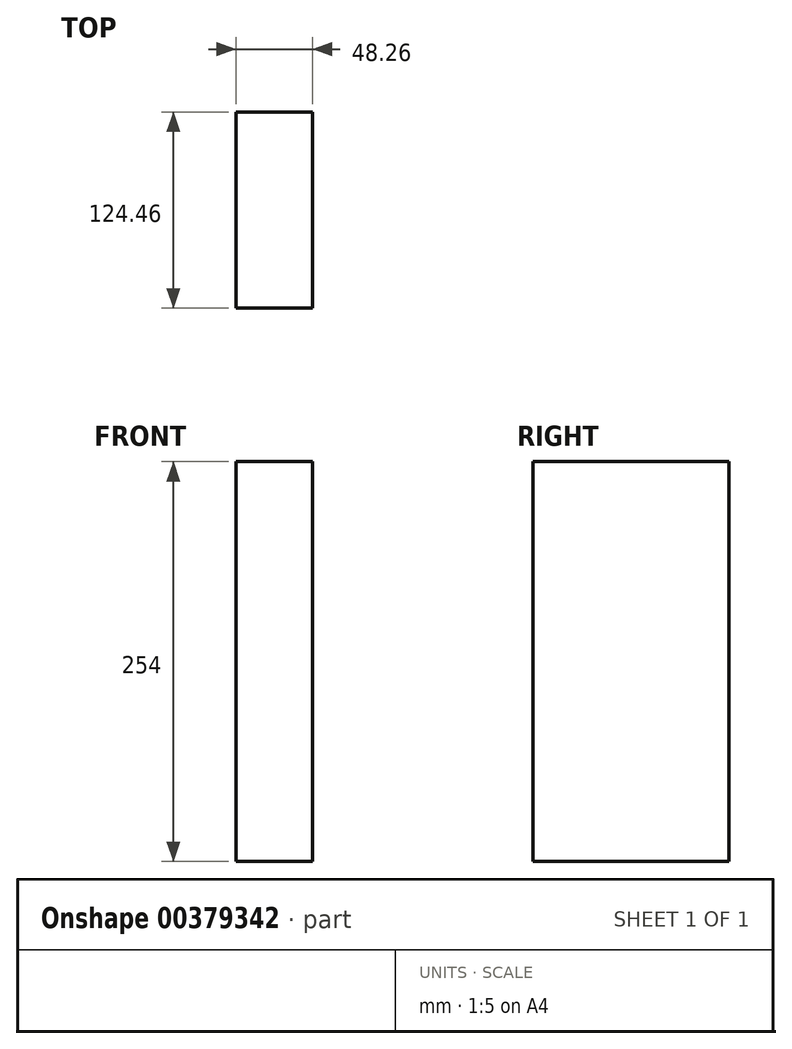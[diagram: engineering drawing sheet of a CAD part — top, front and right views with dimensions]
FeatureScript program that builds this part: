
annotation { "Feature Type Name" : "Feature", "Feature Type Description" : "" }
export const myFeature = defineFeature(function(context is Context, id is Id, definition is map)
    precondition{}
    {
        {
            var Q0;
            Q0=qCreatedBy(makeId("Top.planeOp"),FACE);
            var sketch = newSketch(context, id + "F0", { "sketchPlane" : qUnion([Q0])});
            skLineSegment(sketch, "E0.bottom", {"start": v(-70.95, -145.46) * mm, "end": v(-22.7, -145.46) * mm});
            skLineSegment(sketch, "E0.top", {"start": v(-70.95, -21) * mm, "end": v(-22.7, -21) * mm});
            skLineSegment(sketch, "E0.left", {"start": v(-70.95, -145.46) * mm, "end": v(-70.95, -21) * mm});
            skLineSegment(sketch, "E0.right", {"start": v(-22.7, -145.46) * mm, "end": v(-22.7, -21) * mm});
            skSolve(sketch);
        }
        {
            var Q0;
            Q0=makeQuery(id+"F0.imprint","IMPRINT",FACE,{"disambiguationData":[TD([[makeQuery(id+"F0.imprint","IMPRINT",EDGE,{"derivedFrom":sQuery(id+"F0.wireOp",EDGE,"E0.bottom")}),1.0]])]});
            extrude(context, id + "F1", {"entities" : qUnion([Q0]), "depth" : 254 * mm});
        }
    });
